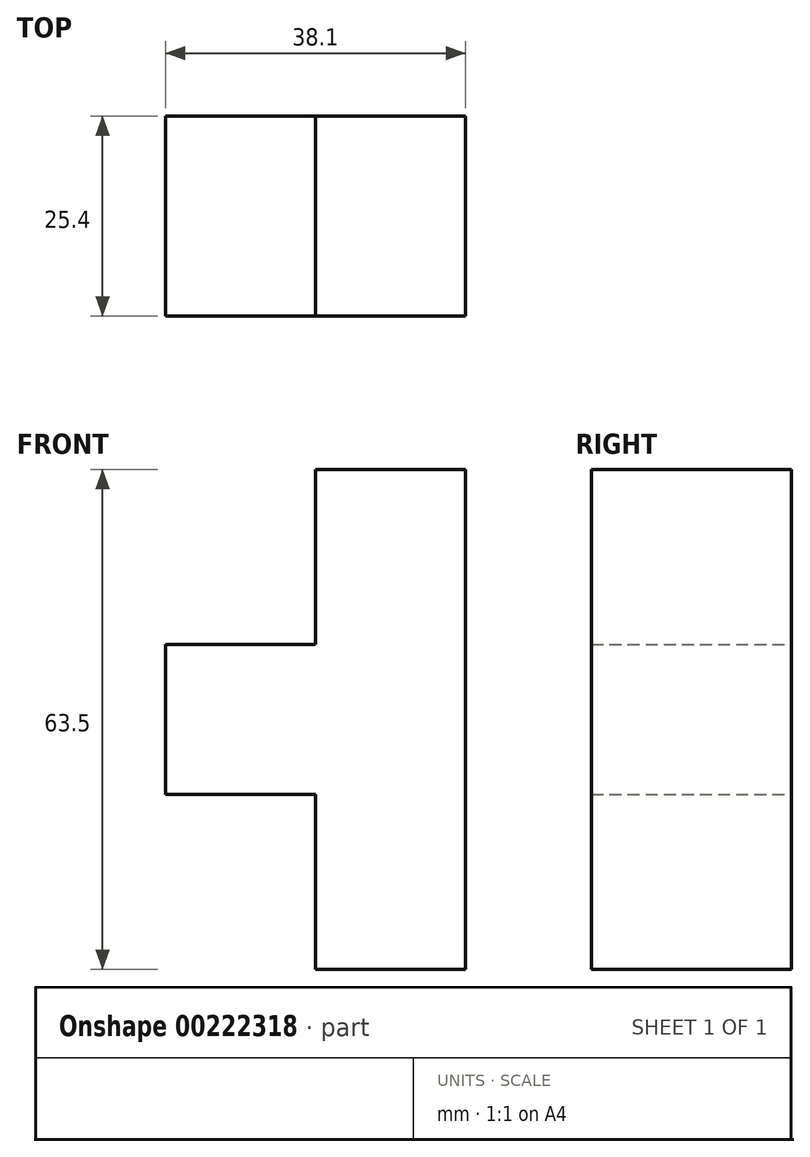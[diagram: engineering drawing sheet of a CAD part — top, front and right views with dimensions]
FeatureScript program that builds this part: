
annotation { "Feature Type Name" : "Feature", "Feature Type Description" : "" }
export const myFeature = defineFeature(function(context is Context, id is Id, definition is map)
    precondition{}
    {
        {
            var Q0;
            Q0=qCreatedBy(makeId("Front.planeOp"),FACE);
            var sketch = newSketch(context, id + "F0", { "sketchPlane" : qUnion([Q0])});
            skLineSegment(sketch, "E0.bottom", {"start": v(-33.02, 13.49) * mm, "end": v(-52.07, 13.49) * mm});
            skLineSegment(sketch, "E0.top", {"start": v(-33.02, 76.99) * mm, "end": v(-52.07, 76.99) * mm});
            skLineSegment(sketch, "E0.left", {"start": v(-33.02, 13.49) * mm, "end": v(-33.02, 76.99) * mm});
            skLineSegment(sketch, "E0.right", {"start": v(-52.07, 13.49) * mm, "end": v(-52.07, 76.99) * mm});
            skPoint(sketch, "E0.middle", {"position": v(-42.54, 45.24) * mm});
            skLineSegment(sketch, "E1.bottom", {"start": v(-52.07, 35.74) * mm, "end": v(-71.12, 35.74) * mm});
            skLineSegment(sketch, "E1.top", {"start": v(-52.07, 54.79) * mm, "end": v(-71.12, 54.79) * mm});
            skLineSegment(sketch, "E1.left", {"start": v(-52.07, 35.74) * mm, "end": v(-52.07, 54.79) * mm});
            skLineSegment(sketch, "E1.right", {"start": v(-71.12, 35.74) * mm, "end": v(-71.12, 54.79) * mm});
            skPoint(sketch, "E1.middle", {"position": v(-61.6, 45.26) * mm});
            skSolve(sketch);
        }
        {
            var Q0;
            Q0 = qSketchRegion(id + "F0", true);
            extrude(context, id + "F1", {"entities" : qUnion([Q0]), "endBound" : BoundingType.SYMMETRIC, "depth" : 25.4 * mm});
        }
    });
